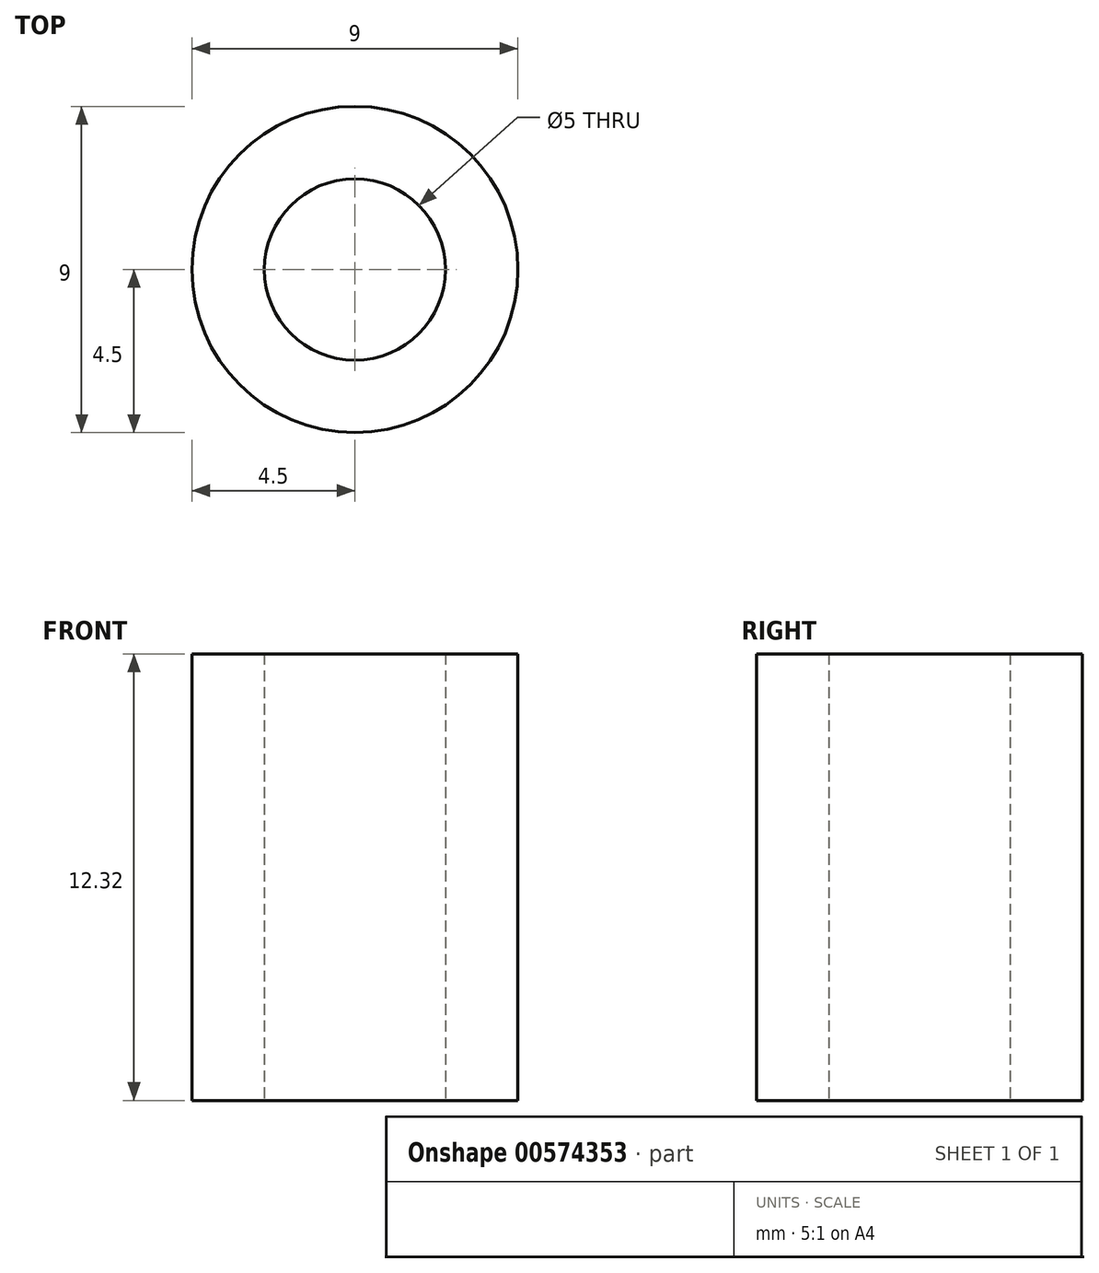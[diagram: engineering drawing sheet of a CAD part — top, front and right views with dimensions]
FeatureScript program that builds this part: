
annotation { "Feature Type Name" : "Feature", "Feature Type Description" : "" }
export const myFeature = defineFeature(function(context is Context, id is Id, definition is map)
    precondition{}
    {
        {
            var Q0;
            Q0=qCreatedBy(makeId("Top.planeOp"),FACE);
            var sketch = newSketch(context, id + "F0", { "sketchPlane" : qUnion([Q0])});
            skCircle(sketch, "E0", {"center": v(0, 0) * mm, "radius": 4.5 * mm});
            skCircle(sketch, "E1", {"center": v(0, 0) * mm, "radius": 2.5 * mm});
            skSolve(sketch);
        }
        {
            var Q0;
            Q0=makeQuery(id+"F0.imprint","IMPRINT",FACE,{"disambiguationData":[TD([[makeQuery(id+"F0.imprint","IMPRINT",EDGE,{"derivedFrom":sQuery(id+"F0.wireOp",EDGE,"E0")}),1.0]])]});
            extrude(context, id + "F1", {"entities" : qUnion([Q0]), "depth" : 20.32 * mm - 8 * mm, "offsetDistance" : 25.4 * mm});
        }
    });
